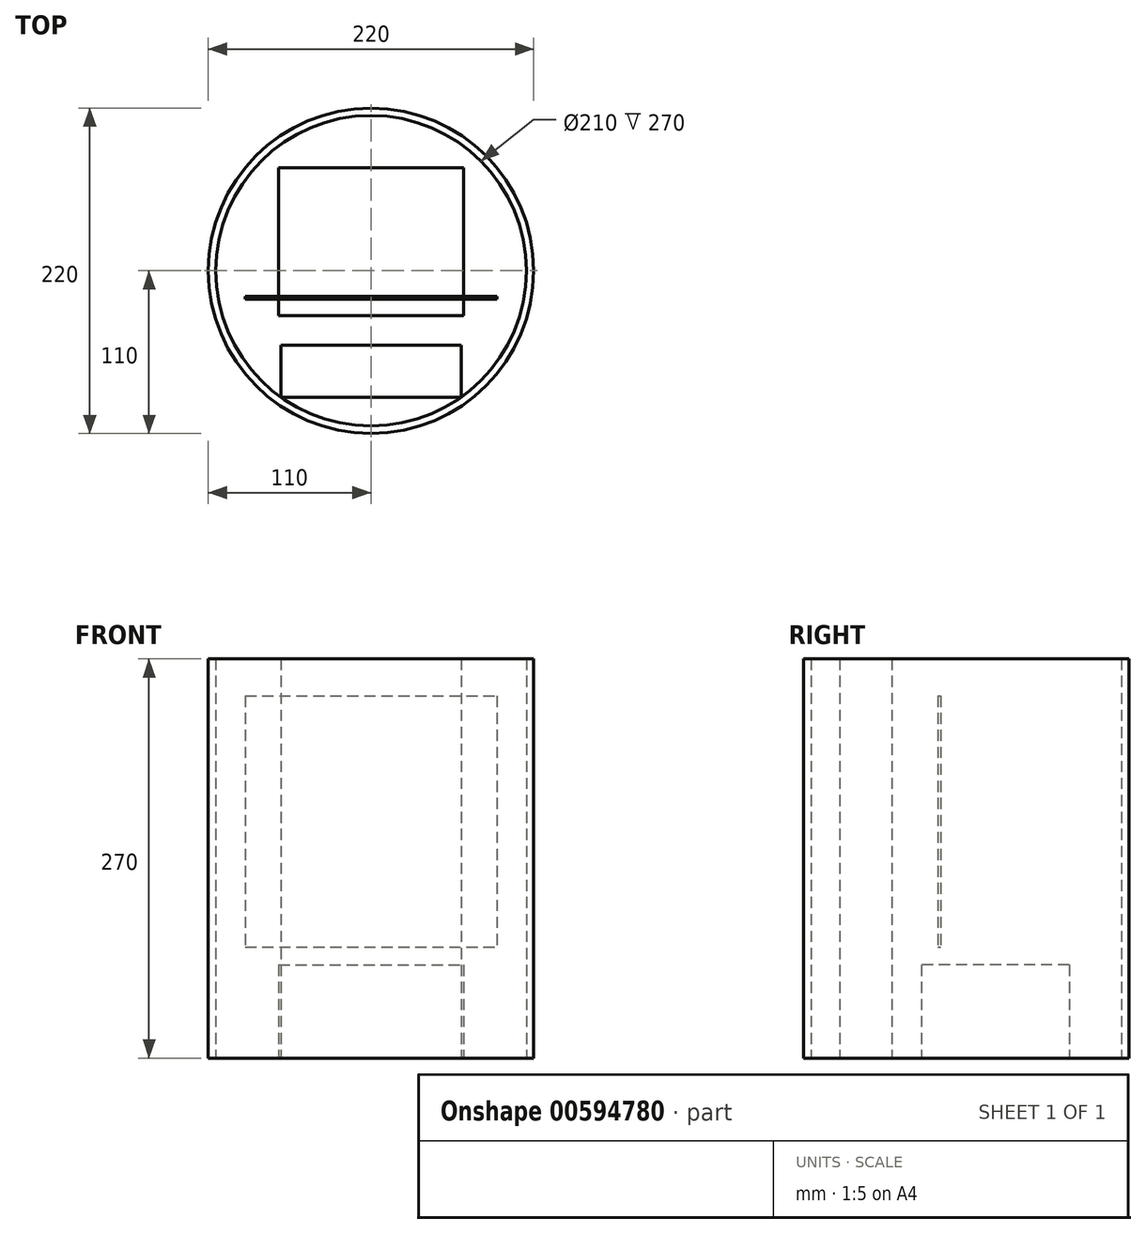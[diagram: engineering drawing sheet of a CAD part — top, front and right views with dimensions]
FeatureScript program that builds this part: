
annotation { "Feature Type Name" : "Feature", "Feature Type Description" : "" }
export const myFeature = defineFeature(function(context is Context, id is Id, definition is map)
    precondition{}
    {
        {
            var Q0;
            Q0=qCreatedBy(makeId("Top.planeOp"),FACE);
            var sketch = newSketch(context, id + "F0", { "sketchPlane" : qUnion([Q0])});
            skCircle(sketch, "E0", {"center": v(0, 0) * mm, "radius": 105 * mm});
            skLineSegment(sketch, "E1", {"start": v(0, -105) * mm, "end": v(0, 0) * mm, "construction": true});
            skLineSegment(sketch, "E2", {"start": v(-85, -19.33) * mm, "end": v(85, -19.33) * mm});
            skPoint(sketch, "E3", {"position": v(0, -19.33) * mm});
            skLineSegment(sketch, "E4", {"start": v(-103.2, -19.33) * mm, "end": v(103.2, -19.33) * mm, "construction": true});
            skLineSegment(sketch, "E5.bottom", {"start": v(-61, -85.46) * mm, "end": v(61, -85.46) * mm});
            skLineSegment(sketch, "E5.top", {"start": v(-61, -50.46) * mm, "end": v(61, -50.46) * mm});
            skLineSegment(sketch, "E5.left", {"start": v(-61, -85.46) * mm, "end": v(-61, -50.46) * mm});
            skLineSegment(sketch, "E5.right", {"start": v(61, -85.46) * mm, "end": v(61, -50.46) * mm});
            skLineSegment(sketch, "E6.bottom", {"start": v(-62.5, 69.54) * mm, "end": v(62.5, 69.54) * mm});
            skLineSegment(sketch, "E6.top", {"start": v(-62.5, -30.46) * mm, "end": v(62.5, -30.46) * mm});
            skLineSegment(sketch, "E6.left", {"start": v(-62.5, 69.54) * mm, "end": v(-62.5, -30.46) * mm});
            skLineSegment(sketch, "E6.right", {"start": v(62.5, 69.54) * mm, "end": v(62.5, -30.46) * mm});
            skLineSegment(sketch, "E7", {"start": v(-62.5, -30.46) * mm, "end": v(62.5, 69.54) * mm, "construction": true});
            skPoint(sketch, "E8", {"position": v(0, 19.54) * mm});
            skSolve(sketch);
        }
        {
            var Q0;
            Q0=qCreatedBy(makeId("Top.planeOp"),FACE);
            var sketch = newSketch(context, id + "F1", { "sketchPlane" : qUnion([Q0])});
            skLineSegment(sketch, "E9.0", {"start": v(-62.5, 69.54) * mm, "end": v(-62.5, -30.46) * mm});
            skLineSegment(sketch, "E10.0", {"start": v(-62.5, 69.54) * mm, "end": v(62.5, 69.54) * mm});
            skLineSegment(sketch, "E11.0", {"start": v(62.5, 69.54) * mm, "end": v(62.5, -30.46) * mm});
            skLineSegment(sketch, "E12.0", {"start": v(-62.5, -30.46) * mm, "end": v(62.5, -30.46) * mm});
            skSolve(sketch);
        }
        {
            var Q0;
            Q0 = qSketchRegion(id + "F1", true);
            extrude(context, id + "F2", {"entities" : qUnion([Q0]), "depth" : 63 * mm, "offsetDistance" : 25 * mm});
        }
        {
            var Q0;
            Q0=qCreatedBy(makeId("Top.planeOp"),FACE);
            cPlane(context, id + "F3", {"entities" : qUnion([Q0]), "cplaneType" : CPlaneType.OFFSET, "offset" : 75 * mm, "width" : 150 * mm, "height" : 150 * mm});
        }
        {
            var Q0;
            Q0=qCreatedBy(id+"F3.planeOp",FACE);
            var sketch = newSketch(context, id + "F4", { "sketchPlane" : qUnion([Q0])});
            skLineSegment(sketch, "E13.0", {"start": v(-85, -19.33) * mm, "end": v(85, -19.33) * mm});
            skLineSegment(sketch, "E14", {"start": v(-85, -19.33) * mm, "end": v(-85, -17.33) * mm});
            skLineSegment(sketch, "E15", {"start": v(-85, -17.33) * mm, "end": v(85, -17.33) * mm});
            skLineSegment(sketch, "E16", {"start": v(85, -17.33) * mm, "end": v(85, -19.33) * mm});
            skSolve(sketch);
        }
        {
            var Q0;
            Q0 = qSketchRegion(id + "F4", true);
            extrude(context, id + "F5", {"entities" : qUnion([Q0]), "depth" : 170 * mm, "offsetDistance" : 25 * mm});
        }
        {
            var Q0;
            Q0=makeQuery(id+"F0.imprint","IMPRINT",FACE,{"disambiguationData":[TD([[makeQuery(id+"F0.imprint","IMPRINT",EDGE,{"derivedFrom":sQuery(id+"F0.wireOp",EDGE,"E5.bottom")}),1.0]])]});
            extrude(context, id + "F6", {"entities" : qUnion([Q0]), "depth" : 270 * mm, "offsetDistance" : 25 * mm});
        }
        {
            var Q0;
            Q0=qCreatedBy(makeId("Top.planeOp"),FACE);
            var sketch = newSketch(context, id + "F7", { "sketchPlane" : qUnion([Q0])});
            skCircle(sketch, "E17", {"center": v(0, 0) * mm, "radius": 105 * mm});
            skCircle(sketch, "E18", {"center": v(0, 0) * mm, "radius": 110 * mm});
            skSolve(sketch);
        }
        {
            var Q0;
            Q0=makeQuery(id+"F7.imprint","IMPRINT",FACE,{"disambiguationData":[TD([[makeQuery(id+"F7.imprint","IMPRINT",EDGE,{"derivedFrom":sQuery(id+"F7.wireOp",EDGE,"E17")}),-1.0]])]});
            extrude(context, id + "F8", {"entities" : qUnion([Q0]), "depth" : 270 * mm, "offsetDistance" : 25 * mm});
        }
    });
